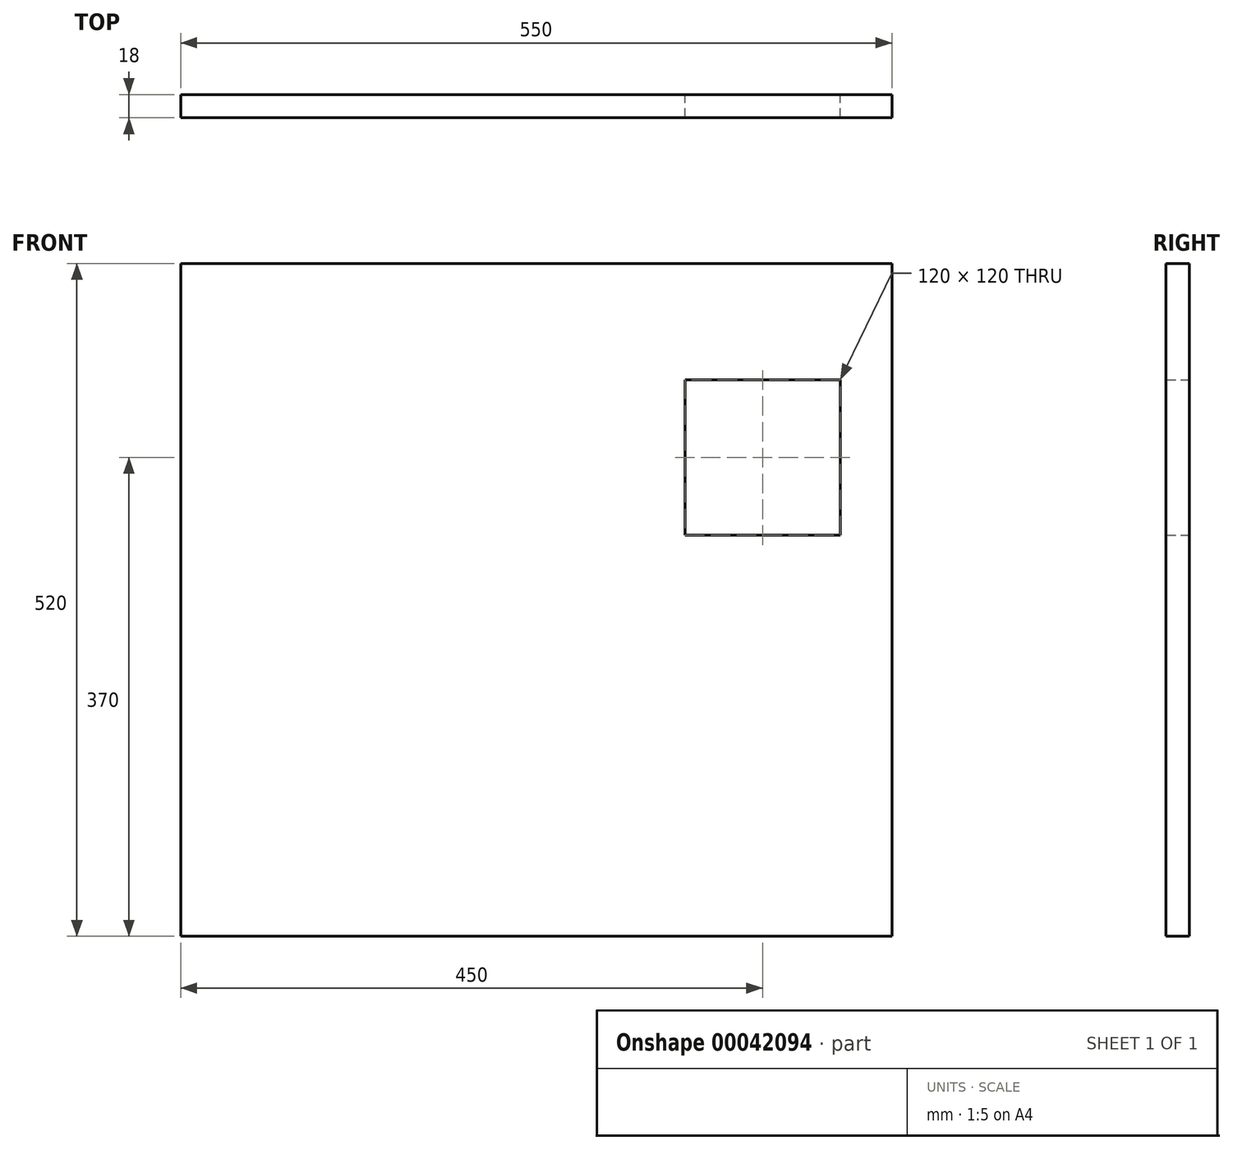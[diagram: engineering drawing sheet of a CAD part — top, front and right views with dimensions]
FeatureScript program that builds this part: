
annotation { "Feature Type Name" : "Feature", "Feature Type Description" : "" }
export const myFeature = defineFeature(function(context is Context, id is Id, definition is map)
    precondition{}
    {
        {
            var Q0;
            Q0=qCreatedBy(makeId("Front.planeOp"),FACE);
            var sketch = newSketch(context, id + "F0", { "sketchPlane" : qUnion([Q0])});
            skLineSegment(sketch, "E0.rect.bottom", {"start": v(275, -260) * mm, "end": v(-275, -260) * mm});
            skLineSegment(sketch, "E0.rect.top", {"start": v(275, 260) * mm, "end": v(-275, 260) * mm});
            skLineSegment(sketch, "E0.rect.left", {"start": v(275, -260) * mm, "end": v(275, 260) * mm});
            skLineSegment(sketch, "E0.rect.right", {"start": v(-275, -260) * mm, "end": v(-275, 260) * mm});
            skPoint(sketch, "E0.rect.middle", {"position": v(0, 0) * mm});
            skLineSegment(sketch, "E1", {"start": v(-275, -210) * mm, "end": v(275, -210) * mm});
            skLineSegment(sketch, "E2", {"start": v(-275, 210) * mm, "end": v(275, 210) * mm});
            skLineSegment(sketch, "E3.bottom", {"start": v(115, 170) * mm, "end": v(235, 170) * mm});
            skLineSegment(sketch, "E3.top", {"start": v(115, 50) * mm, "end": v(235, 50) * mm});
            skLineSegment(sketch, "E3.left", {"start": v(115, 170) * mm, "end": v(115, 50) * mm});
            skLineSegment(sketch, "E3.right", {"start": v(235, 170) * mm, "end": v(235, 50) * mm});
            skSolve(sketch);
        }
        {
            var Q0;
            Q0 = qSketchRegion(id + "F0", true);
            extrude(context, id + "F1", {"entities" : qUnion([Q0]), "depth" : 18 * mm});
        }
    });
